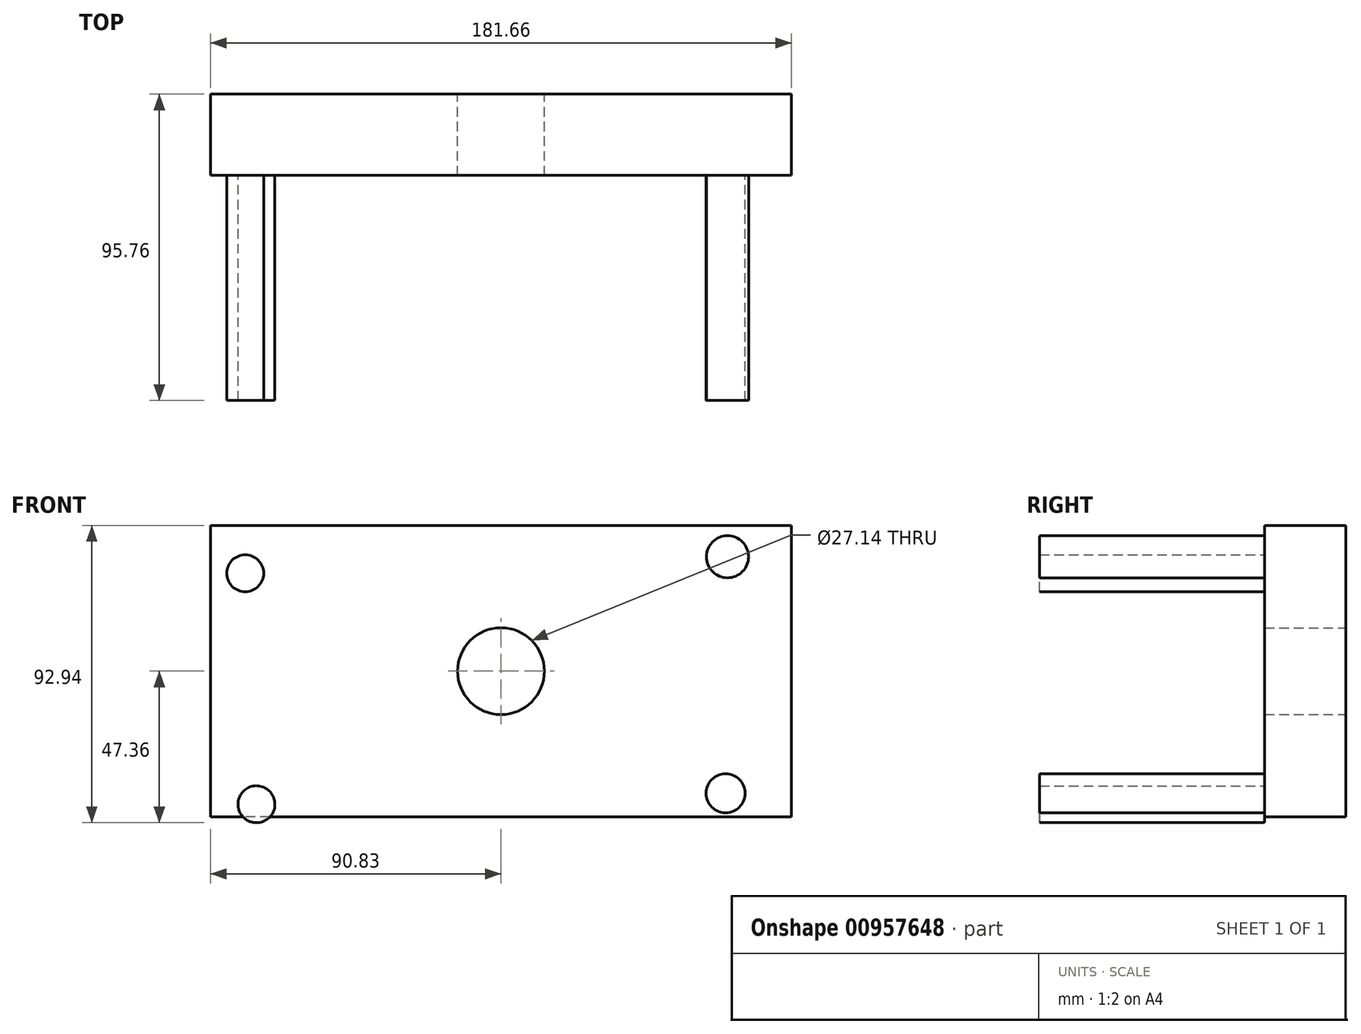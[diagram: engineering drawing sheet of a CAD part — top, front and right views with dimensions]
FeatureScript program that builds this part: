
annotation { "Feature Type Name" : "Feature", "Feature Type Description" : "" }
export const myFeature = defineFeature(function(context is Context, id is Id, definition is map)
    precondition{}
    {
        {
            var Q0;
            Q0=qCreatedBy(makeId("Front.planeOp"),FACE);
            var sketch = newSketch(context, id + "F0", { "sketchPlane" : qUnion([Q0])});
            skLineSegment(sketch, "E0.bottom", {"start": v(90.83, -45.58) * mm, "end": v(-90.83, -45.58) * mm});
            skLineSegment(sketch, "E0.top", {"start": v(90.83, 45.58) * mm, "end": v(-90.83, 45.58) * mm});
            skLineSegment(sketch, "E0.left", {"start": v(90.83, -45.58) * mm, "end": v(90.83, 45.58) * mm});
            skLineSegment(sketch, "E0.right", {"start": v(-90.83, -45.58) * mm, "end": v(-90.83, 45.58) * mm});
            skPoint(sketch, "E0.middle", {"position": v(0, 0) * mm});
            skCircle(sketch, "E1", {"center": v(0, 0) * mm, "radius": 31.54 * mm});
            skCircle(sketch, "E2", {"center": v(0, 0) * mm, "radius": 13.57 * mm});
            skSolve(sketch);
        }
        {
            var Q0;
            Q0=makeQuery(id+"F0.imprint","IMPRINT",FACE,{"disambiguationData":[TD([[makeQuery(id+"F0.imprint","IMPRINT",EDGE,{"derivedFrom":sQuery(id+"F0.wireOp",EDGE,"E1")}),1.0]])]});
            var Q1;
            Q1=makeQuery(id+"F0.imprint","IMPRINT",FACE,{"disambiguationData":[TD([[makeQuery(id+"F0.imprint","IMPRINT",EDGE,{"derivedFrom":sQuery(id+"F0.wireOp",EDGE,"E0.bottom")}),-1.0]])]});
            extrude(context, id + "F1", {"entities" : qUnion([Q0, Q1]), "depth" : 25.4 * mm, "offsetDistance" : 25.4 * mm});
        }
        {
            var Q0;
            Q0=makeQuery(id+"F1.opExtrude","CAP_FACE",FACE,{"disambiguationData":[OSD([sQuery(id+"F0.wireOp",EDGE,"E0.bottom"),sQuery(id+"F0.wireOp",EDGE,"E0.top"),sQuery(id+"F0.wireOp",EDGE,"E0.left"),sQuery(id+"F0.wireOp",EDGE,"E0.right"),sQuery(id+"F0.wireOp",EDGE,"E2")])],"isStart":false});
            var sketch = newSketch(context, id + "F2", { "sketchPlane" : qUnion([Q0])});
            skCircle(sketch, "E3", {"center": v(70.24, -38.16) * mm, "radius": 6.1 * mm});
            skCircle(sketch, "E4", {"center": v(70.83, 35.76) * mm, "radius": 6.58 * mm});
            skCircle(sketch, "E5", {"center": v(-76.45, -41.59) * mm, "radius": 5.77 * mm});
            skCircle(sketch, "E6", {"center": v(-79.96, 30.6) * mm, "radius": 5.77 * mm});
            skSolve(sketch);
        }
        {
            var Q0;
            Q0 = qSketchRegion(id + "F2", true);
            extrude(context, id + "F3", {"entities" : qUnion([Q0]), "operationType" : NewBodyOperationType.ADD, "depth" : 70.36 * mm, "offsetDistance" : 25.4 * mm});
        }
    });
